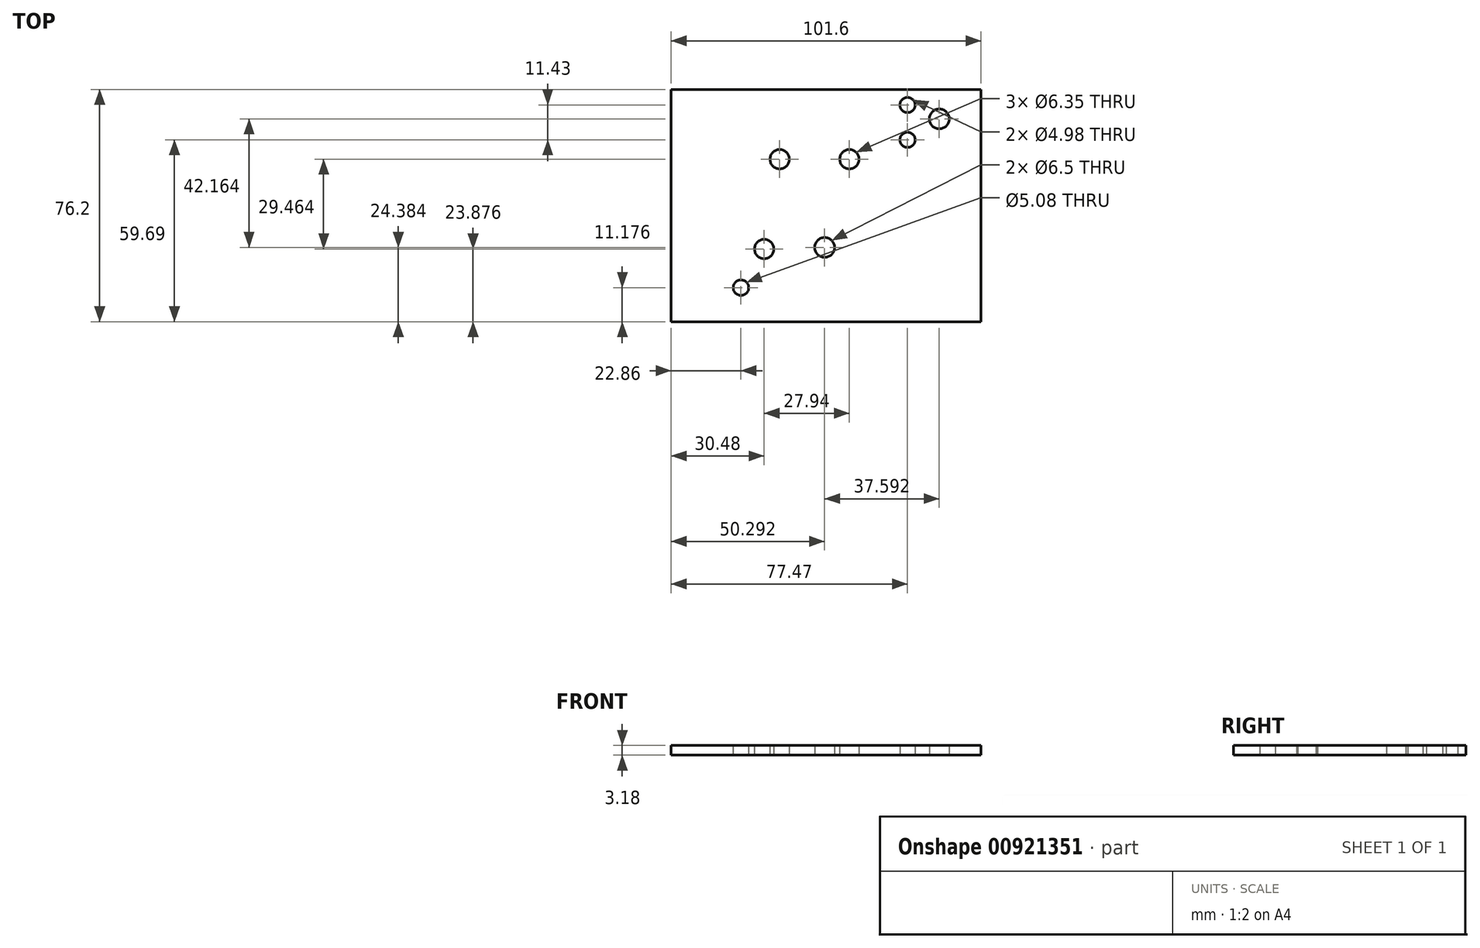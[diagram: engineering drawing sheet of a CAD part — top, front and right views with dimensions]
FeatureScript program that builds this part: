
annotation { "Feature Type Name" : "Feature", "Feature Type Description" : "" }
export const myFeature = defineFeature(function(context is Context, id is Id, definition is map)
    precondition{}
    {
        {
            var Q0;
            Q0=qCreatedBy(makeId("Top.planeOp"),FACE);
            var sketch = newSketch(context, id + "F0", { "sketchPlane" : qUnion([Q0])});
            skLineSegment(sketch, "E0.bottom", {"start": v(0, 0) * mm, "end": v(101.6, 0) * mm});
            skLineSegment(sketch, "E0.top", {"start": v(0, 76.2) * mm, "end": v(101.6, 76.2) * mm});
            skLineSegment(sketch, "E0.left", {"start": v(0, 0) * mm, "end": v(0, 76.2) * mm});
            skLineSegment(sketch, "E0.right", {"start": v(101.6, 0) * mm, "end": v(101.6, 76.2) * mm});
            skSolve(sketch);
        }
        {
            var Q0;
            Q0=qCreatedBy(makeId("Top.planeOp"),FACE);
            var sketch = newSketch(context, id + "F1", { "sketchPlane" : qUnion([Q0])});
            skCircle(sketch, "E1", {"center": v(22.86, 11.18) * mm, "radius": 2.54 * mm});
            skSolve(sketch);
        }
        {
            var Q0;
            Q0=qCreatedBy(makeId("Top.planeOp"),FACE);
            var sketch = newSketch(context, id + "F2", { "sketchPlane" : qUnion([Q0])});
            skCircle(sketch, "E2", {"center": v(30.48, 23.88) * mm, "radius": 3.18 * mm});
            skCircle(sketch, "E3", {"center": v(35.56, 53.34) * mm, "radius": 3.18 * mm});
            skCircle(sketch, "E4", {"center": v(58.42, 53.34) * mm, "radius": 3.18 * mm});
            skSolve(sketch);
        }
        {
            var Q0;
            Q0=qCreatedBy(makeId("Top.planeOp"),FACE);
            var sketch = newSketch(context, id + "F3", { "sketchPlane" : qUnion([Q0])});
            skCircle(sketch, "E5", {"center": v(50.3, 24.38) * mm, "radius": 3.25 * mm});
            skCircle(sketch, "E6", {"center": v(87.88, 66.55) * mm, "radius": 3.25 * mm});
            skSolve(sketch);
        }
        {
            var Q0;
            Q0=qCreatedBy(makeId("Top.planeOp"),FACE);
            var sketch = newSketch(context, id + "F4", { "sketchPlane" : qUnion([Q0])});
            skCircle(sketch, "E7", {"center": v(77.47, 71.12) * mm, "radius": 2.49 * mm});
            skCircle(sketch, "E8", {"center": v(77.47, 59.7) * mm, "radius": 2.49 * mm});
            skSolve(sketch);
        }
        {
            var Q0;
            Q0 = qSketchRegion(id + "F0", true);
            extrude(context, id + "F5", {"entities" : qUnion([Q0]), "depth" : 3.17 * mm, "offsetDistance" : 25.4 * mm});
        }
        {
            var Q0;
            Q0 = qSketchRegion(id + "F1", true);
            var Q1;
            Q1 = qSketchRegion(id + "F2", true);
            var Q2;
            Q2 = qSketchRegion(id + "F3", true);
            var Q3;
            Q3 = qSketchRegion(id + "F4", true);
            extrude(context, id + "F6", {"entities" : qUnion([Q0, Q1, Q2, Q3]), "operationType" : NewBodyOperationType.REMOVE, "endBound" : BoundingType.THROUGH_ALL, "depth" : 25.4 * mm, "offsetDistance" : 25.4 * mm});
        }
    });
